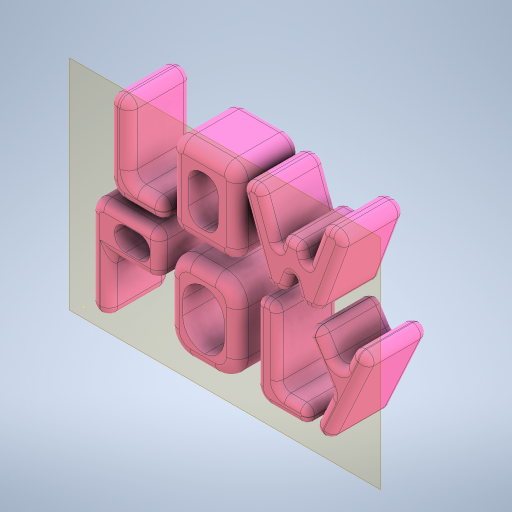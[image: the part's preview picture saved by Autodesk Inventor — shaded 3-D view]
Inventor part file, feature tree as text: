
AUTODESK INVENTOR PART (.ipt)
format: ipt  version: 2024.1 (Build 281209000, 209)  size: 949,248 bytes
history: native  units: mm
features: fillet x23, sketch x4, extrude x3, projected_geometry x1
ambient origin geometry x8: Origin, YZ Plane, XZ Plane, XY Plane, X Axis, Y Axis, Z Axis, Center Point
bodies: Solid2 (feature_tree)
feature tree (31):
  extrude  "Extrusion6"  Depth=10.0mm TaperAngle=0.0deg
  extrude  "Extrusion1"  Depth=90.0mm
  extrude  "Extrusion7"  Depth=1.0mm
  fillet  "Fillet1"  Radius=19.198622mm
  fillet  "Fillet2"  Radius=10.0mm
  fillet  "Fillet3"  Radius=28.0mm
  fillet  "Fillet4"  [1 undecoded]
  fillet  "Fillet5"  Radius=4.0mm
  fillet  "Fillet6"  Radius=5.0mm
  fillet  "Fillet7"  Radius=5.0mm
  fillet  "Fillet8"  Radius=10.0mm
  fillet  "Fillet9"  Radius=10.0mm
  fillet  "Fillet10"  Radius=5.0mm
  fillet  "Fillet11"  Radius=3.5mm
  fillet  "Fillet12"  Radius=3.0mm
  fillet  "Fillet13"  Radius=6.0mm
  fillet  "Fillet14"  Radius=3.5mm
  fillet  "Fillet15"  Radius=3.5mm
  fillet  "Fillet16"  Radius=4.0mm
  fillet  "Fillet17"  Radius=4.0mm
  fillet  "Fillet18"  Radius=7.0mm
  fillet  "Fillet19"  Radius=6.0mm
  fillet  "Fillet20"  Radius=6.0mm
  fillet  "Fillet21"  Radius=5.0mm
  fillet  "Fillet22"  Radius=4.0mm
  fillet  "Fillet23"  Radius=1.0mm
  sketch  "Sketch8"  dims[d61=3.0mm d62=3.0mm d63=19.198622mm d64=7.056118mm d65=7.5mm d66=6.0mm d67=3.0mm d69=3.931055mm d70=3.9mm]
  sketch  "Sketch1"  dims[d0=40.0mm d4=10.0mm d5=0.0mm]
  sketch  "Sketch6"  dims[d24=160.0mm d25=90.0mm]
  projected_geometry  "Projected Loop1"
  sketch  "Sketch7"  dims[d26=90.0mm d27=0.0mm d28=19.198622mm d29=19.198622mm d31=10.0mm d39=28.0mm d40=0.0mm d41=0.0mm d42=4.0mm d43=5.0mm d44=5.0mm d45=10.0mm d46=10.0mm d47=5.0mm d48=3.5mm d49=3.0mm d50=6.0mm d51=3.5mm d52=3.5mm d53=4.0mm d54=4.0mm d55=7.0mm d56=6.0mm d57=6.0mm d58=5.0mm d59=4.0mm d60=1.0mm]
note: 1 required parameter value undecoded (feature->parameter linkage not recoverable at this tier; creation-order binding heuristic only, values carry confidence <= 0.55)
